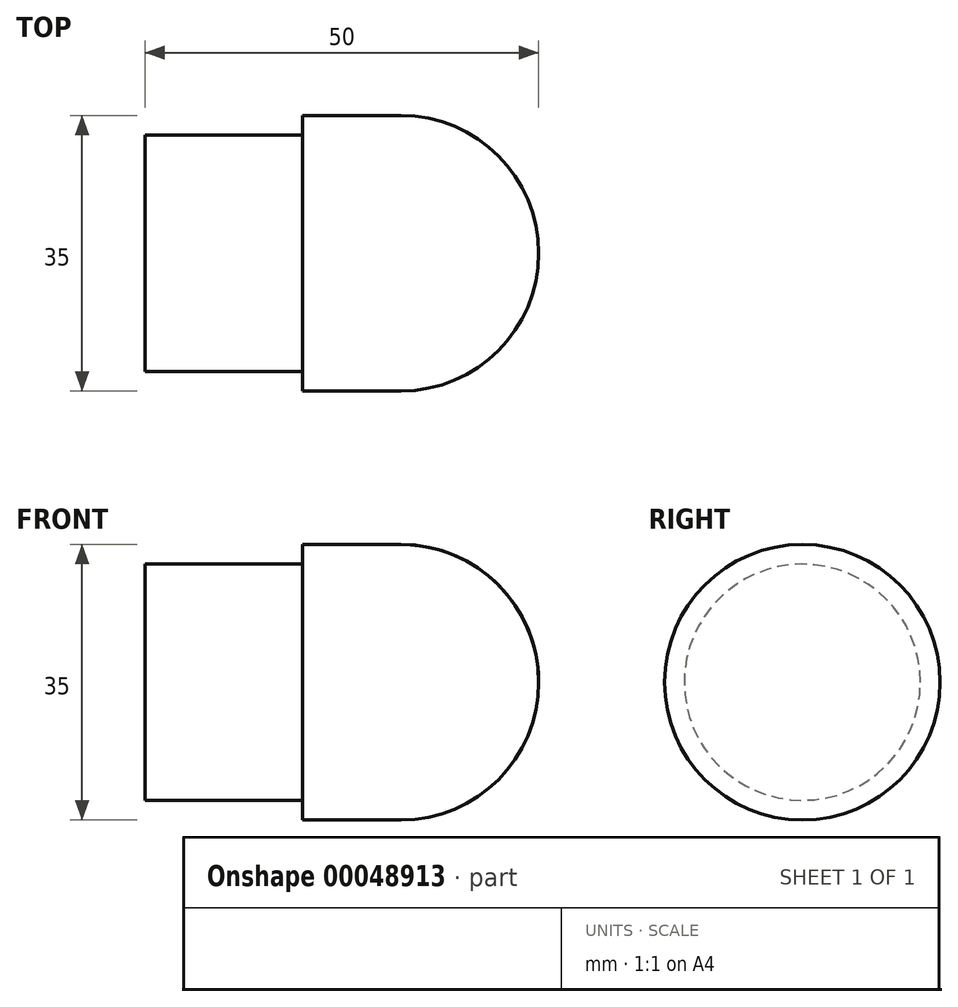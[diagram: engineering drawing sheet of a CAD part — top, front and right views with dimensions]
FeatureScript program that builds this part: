
annotation { "Feature Type Name" : "Feature", "Feature Type Description" : "" }
export const myFeature = defineFeature(function(context is Context, id is Id, definition is map)
    precondition{}
    {
        {
            var Q0;
            Q0=qCreatedBy(makeId("Front.planeOp"),FACE);
            var sketch = newSketch(context, id + "F0", { "sketchPlane" : qUnion([Q0])});
            skLineSegment(sketch, "E0", {"start": v(0, 15) * mm, "end": v(20, 15) * mm});
            skLineSegment(sketch, "E1", {"start": v(20, 15) * mm, "end": v(20, 17.5) * mm});
            skLineSegment(sketch, "E2", {"start": v(20, 17.5) * mm, "end": v(32.5, 17.5) * mm});
            skArc(sketch, "E3", {"start": v(32.5, 17.5) * mm, "mid": v(44.87, 12.37) * mm, "end": v(50, 0) * mm});
            skLineSegment(sketch, "E4", {"start": v(50, 0) * mm, "end": v(0, 0) * mm});
            skLineSegment(sketch, "E5", {"start": v(0, 0) * mm, "end": v(0, 15) * mm});
            skSolve(sketch);
        }
        {
            var Q0;
            Q0=makeQuery(id+"F0.imprint","IMPRINT",FACE,{"disambiguationData":[TD([[makeQuery(id+"F0.imprint","IMPRINT",EDGE,{"derivedFrom":sQuery(id+"F0.wireOp",EDGE,"E0")}),-1.0]])]});
            var Q1;
            Q1=sQuery(id+"F0.wireOp",EDGE,"E4");
            revolve(context, id + "F1", {"entities" : qUnion([Q0]), "axis" : qUnion([Q1]), "revolveType" : RevolveType.FULL});
        }
    });
